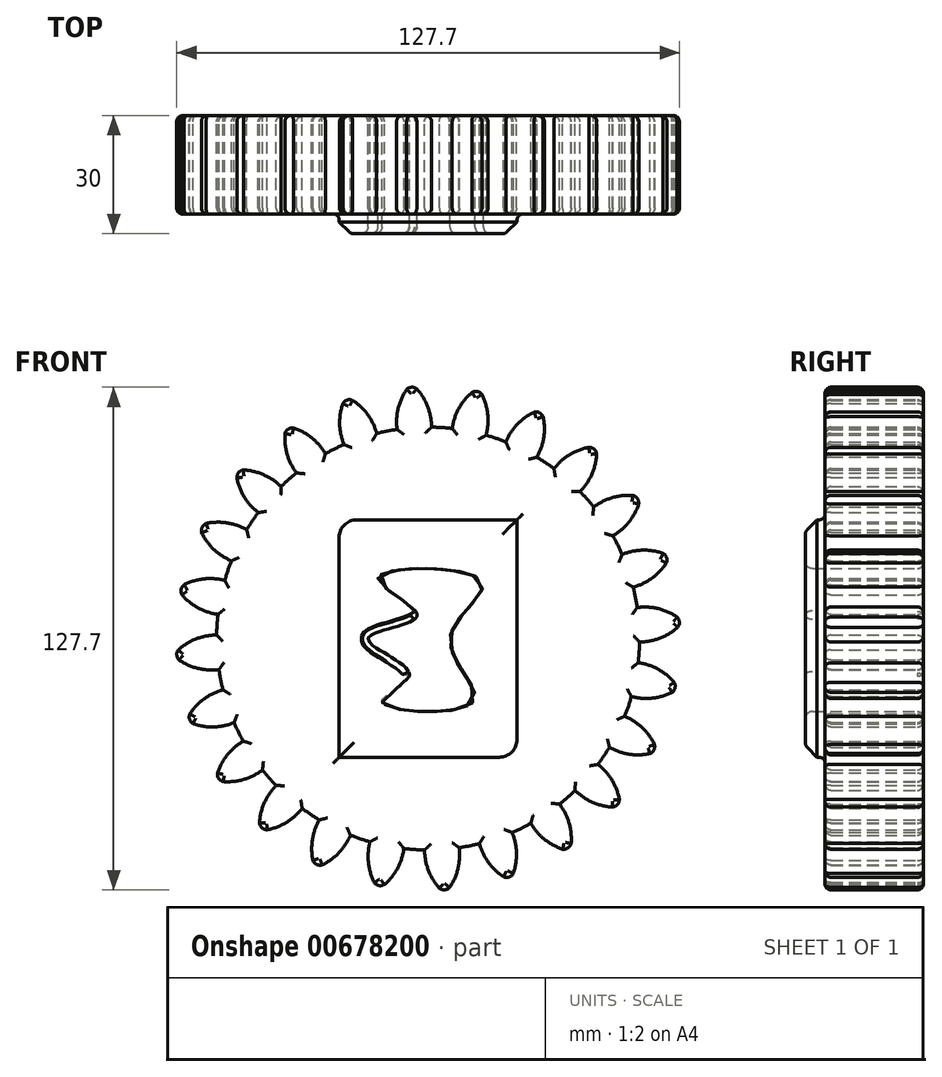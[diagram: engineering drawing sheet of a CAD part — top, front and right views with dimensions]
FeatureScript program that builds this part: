
annotation { "Feature Type Name" : "Feature", "Feature Type Description" : "" }
export const myFeature = defineFeature(function(context is Context, id is Id, definition is map)
    precondition{}
    {
        {
            var Q0;
            Q0=qCreatedBy(makeId("Front.planeOp"),FACE);
            var sketch = newSketch(context, id + "F0", { "sketchPlane" : qUnion([Q0])});
            skCircle(sketch, "E0", {"center": v(0, 0) * mm, "radius": 53.72 * mm});
            skCircle(sketch, "E1", {"center": v(0, 0) * mm, "radius": 58.67 * mm, "construction": true});
            skCircle(sketch, "E2", {"center": v(0, 0) * mm, "radius": 63.5 * mm, "construction": true});
            skLineSegment(sketch, "E3", {"start": v(0, 0) * mm, "end": v(0, 95.08) * mm, "construction": true});
            skLineSegment(sketch, "E4", {"start": v(0, 0) * mm, "end": v(-6.3, 96.03) * mm, "construction": true});
            skLineSegment(sketch, "E5", {"start": v(0, 63.95) * mm, "end": v(0, 63.5) * mm, "construction": true});
            skLineSegment(sketch, "E6", {"start": v(0, 58.67) * mm, "end": v(-63.97, 58.67) * mm, "construction": true});
            skLineSegment(sketch, "E7", {"start": v(0, 58.67) * mm, "end": v(-64.16, 35.32) * mm, "construction": true});
            skCircle(sketch, "E8", {"center": v(0, 0) * mm, "radius": 55.14 * mm, "construction": true});
            skCircle(sketch, "E9", {"center": v(0, 58.67) * mm, "radius": 14.6 * mm, "construction": true});
            skCircle(sketch, "E10", {"center": v(-13.72, 53.68) * mm, "radius": 14.6 * mm, "construction": true});
            skArc(sketch, "E11", {"start": v(0, 58.67) * mm, "mid": v(-1.2, 61.2) * mm, "end": v(-2.86, 63.44) * mm});
            skArc(sketch, "E12", {"start": v(0.88, 53.71) * mm, "mid": v(0.66, 56.23) * mm, "end": v(0, 58.67) * mm});
            skArc(sketch, "E13.MirrorCS", {"start": v(-7.66, 58.17) * mm, "mid": v(-6.8, 60.83) * mm, "end": v(-5.45, 63.27) * mm});
            skArc(sketch, "E14.MirrorCS", {"start": v(-7.88, 53.14) * mm, "mid": v(-7.99, 55.67) * mm, "end": v(-7.66, 58.17) * mm});
            skArc(sketch, "E15", {"start": v(-2.86, 63.44) * mm, "mid": v(-4.18, 63.85) * mm, "end": v(-5.45, 63.27) * mm});
            skLineSegment(sketch, "E16.bottom", {"start": v(22.6, 30.17) * mm, "end": v(-18.1, 30.17) * mm});
            skLineSegment(sketch, "E16.top", {"start": v(18.1, -30.17) * mm, "end": v(-22.6, -30.17) * mm});
            skLineSegment(sketch, "E16.left", {"start": v(22.6, 30.17) * mm, "end": v(22.6, -25.67) * mm});
            skLineSegment(sketch, "E16.right", {"start": v(-22.6, 25.67) * mm, "end": v(-22.6, -30.17) * mm});
            skFitSpline(sketch, "E17", {"points": [v(-11.69, -16.1) * mm, v(11.42, -16.15) * mm, v(5.58, 0) * mm, v(13.67, 14.65) * mm, v(-12.75, 15.4) * mm, v(-2.8, 5.83) * mm, v(-15.25, 0) * mm, v(-4.75, -9.12) * mm, v(-11.69, -16.1) * mm]});
            skPoint(sketch, "E18.visualSharp", {"position": v(-22.6, 30.17) * mm});
            skArc(sketch, "E18.filletArc", {"start": v(-18.1, 30.17) * mm, "mid": v(-21.28, 28.85) * mm, "end": v(-22.6, 25.67) * mm});
            skPoint(sketch, "E19.visualSharp", {"position": v(22.6, -30.17) * mm});
            skArc(sketch, "E19.filletArc", {"start": v(18.1, -30.17) * mm, "mid": v(21.28, -28.85) * mm, "end": v(22.6, -25.67) * mm});
            skSolve(sketch);
        }
        {
            var Q0;
            {var subQ0=sQuery(id+"F0.wireOp",EDGE,"E0");var subQ1=makeQuery(id+"F0.imprint","INTERSECT",VERTEX,{"derivedFrom":[subQ0,sQuery(id+"F0.wireOp",EDGE,"E12")]});Q0=makeQuery(id+"F0.imprint","IMPRINT",FACE,{"disambiguationData":[TD([[makeQuery(id+"F0.imprint","IMPRINT",EDGE,{"disambiguationData":[TD([[subQ1,-1.0]])],"derivedFrom":subQ0}),1.0]])]});}
            var Q1;
            Q1=makeQuery(id+"F0.imprint","IMPRINT",FACE,{"disambiguationData":[TD([[makeQuery(id+"F0.imprint","IMPRINT",EDGE,{"derivedFrom":sQuery(id+"F0.wireOp",EDGE,"E11")}),1.0]])]});
            extrude(context, id + "F1", {"entities" : qUnion([Q0, Q1]), "depth" : 25 * mm, "offsetDistance" : 25 * mm});
        }
        {
            var Q0;
            Q0=makeQuery(id+"F1.opExtrude","SWEPT_BODY",BODY,{"disambiguationData":[OSD([sQuery(id+"F0.wireOp",EDGE,"E0"),sQuery(id+"F0.wireOp",EDGE,"E11"),sQuery(id+"F0.wireOp",EDGE,"E12"),sQuery(id+"F0.wireOp",EDGE,"E13.MirrorCS"),sQuery(id+"F0.wireOp",EDGE,"E14.MirrorCS"),sQuery(id+"F0.wireOp",EDGE,"E15")])]});
            var Q1;
            Q1=makeQuery(id+"F1.opExtrude","SWEPT_FACE",FACE,{"disambiguationData":[OSD([sQuery(id+"F0.wireOp",EDGE,"E0")])]});
            circularPattern(context, id + "F2", {"entities" : qUnion([Q0]), "axis" : qUnion([Q1]), "angle" : 360 * degree, "instanceCount" : 24, "equalSpace" : true});
        }
        {
            var Q0;
            Q0=makeQuery(id+"F0.imprint","IMPRINT",FACE,{"disambiguationData":[TD([[makeQuery(id+"F0.imprint","IMPRINT",EDGE,{"derivedFrom":sQuery(id+"F0.wireOp",EDGE,"E16.bottom")}),1.0]])]});
            extrude(context, id + "F3", {"entities" : qUnion([Q0]), "operationType" : NewBodyOperationType.ADD, "depth" : 30 * mm, "offsetDistance" : 25 * mm});
        }
        {
            var Q0;
            Q0=makeQuery(id+"F3.opExtrude","CAP_EDGE",EDGE,{"disambiguationData":[OSD([sQuery(id+"F0.wireOp",EDGE,"E16.bottom")])],"isStart":false});
            var Q1;
            Q1=makeQuery(id+"F3.opExtrude","CAP_EDGE",EDGE,{"disambiguationData":[OSD([sQuery(id+"F0.wireOp",EDGE,"E16.right")])],"isStart":false});
            var Q2;
            Q2=makeQuery(id+"F3.opExtrude","CAP_EDGE",EDGE,{"disambiguationData":[OSD([sQuery(id+"F0.wireOp",EDGE,"E16.left")])],"isStart":false});
            var Q3;
            Q3=makeQuery(id+"F3.opExtrude","CAP_EDGE",EDGE,{"disambiguationData":[OSD([sQuery(id+"F0.wireOp",EDGE,"E16.top")])],"isStart":false});
            var Q4;
            Q4=makeQuery(id+"F3.opExtrude","CAP_EDGE",EDGE,{"disambiguationData":[OSD([sQuery(id+"F0.wireOp",EDGE,"E16.bottom")])],"isStart":true});
            var Q5;
            Q5=makeQuery(id+"F3.opExtrude","CAP_EDGE",EDGE,{"disambiguationData":[OSD([sQuery(id+"F0.wireOp",EDGE,"E16.top")])],"isStart":true});
            chamfer(context, id + "F4", {"entities" : qUnion([Q0, Q1, Q2, Q3, Q4, Q5]), "width" : 3 * mm, "tangentPropagation" : true});
        }
        {
            var Q0;
            {var subQ0=sQuery(id+"F0.wireOp",EDGE,"E19.filletArc");var subQ1=sQuery(id+"F0.wireOp",EDGE,"E18.filletArc");var subQ2=sQuery(id+"F0.wireOp",EDGE,"E16.right");var subQ3=sQuery(id+"F0.wireOp",EDGE,"E16.left");var subQ4=sQuery(id+"F0.wireOp",EDGE,"E16.top");var subQ5=sQuery(id+"F0.wireOp",EDGE,"E16.bottom");var subQ6=makeQuery(id+"F1.opExtrude","CAP_FACE",FACE,{"disambiguationData":[OSD([sQuery(id+"F0.wireOp",EDGE,"E0"),sQuery(id+"F0.wireOp",EDGE,"E11"),sQuery(id+"F0.wireOp",EDGE,"E12"),sQuery(id+"F0.wireOp",EDGE,"E13.MirrorCS"),sQuery(id+"F0.wireOp",EDGE,"E14.MirrorCS"),sQuery(id+"F0.wireOp",EDGE,"E15"),subQ5,subQ4,subQ3,subQ2,subQ1,subQ0])],"isStart":true});Q0=makeQuery(id+"F3.boolean.opBoolean","MERGE",FACE,{"derivedFrom":[subQ6,makeQuery(id+"F2.opPattern","COPY",FACE,{"derivedFrom":subQ6,"instanceName":"1"}),makeQuery(id+"F2.opPattern","COPY",FACE,{"derivedFrom":subQ6,"instanceName":"2"}),makeQuery(id+"F2.opPattern","COPY",FACE,{"derivedFrom":subQ6,"instanceName":"3"}),makeQuery(id+"F2.opPattern","COPY",FACE,{"derivedFrom":subQ6,"instanceName":"4"}),makeQuery(id+"F2.opPattern","COPY",FACE,{"derivedFrom":subQ6,"instanceName":"5"}),makeQuery(id+"F2.opPattern","COPY",FACE,{"derivedFrom":subQ6,"instanceName":"6"}),makeQuery(id+"F2.opPattern","COPY",FACE,{"derivedFrom":subQ6,"instanceName":"7"}),makeQuery(id+"F2.opPattern","COPY",FACE,{"derivedFrom":subQ6,"instanceName":"8"}),makeQuery(id+"F2.opPattern","COPY",FACE,{"derivedFrom":subQ6,"instanceName":"9"}),makeQuery(id+"F2.opPattern","COPY",FACE,{"derivedFrom":subQ6,"instanceName":"10"}),makeQuery(id+"F2.opPattern","COPY",FACE,{"derivedFrom":subQ6,"instanceName":"11"}),makeQuery(id+"F2.opPattern","COPY",FACE,{"derivedFrom":subQ6,"instanceName":"12"}),makeQuery(id+"F2.opPattern","COPY",FACE,{"derivedFrom":subQ6,"instanceName":"13"}),makeQuery(id+"F2.opPattern","COPY",FACE,{"derivedFrom":subQ6,"instanceName":"14"}),makeQuery(id+"F2.opPattern","COPY",FACE,{"derivedFrom":subQ6,"instanceName":"15"}),makeQuery(id+"F2.opPattern","COPY",FACE,{"derivedFrom":subQ6,"instanceName":"16"}),makeQuery(id+"F2.opPattern","COPY",FACE,{"derivedFrom":subQ6,"instanceName":"17"}),makeQuery(id+"F2.opPattern","COPY",FACE,{"derivedFrom":subQ6,"instanceName":"18"}),makeQuery(id+"F2.opPattern","COPY",FACE,{"derivedFrom":subQ6,"instanceName":"19"}),makeQuery(id+"F2.opPattern","COPY",FACE,{"derivedFrom":subQ6,"instanceName":"20"}),makeQuery(id+"F2.opPattern","COPY",FACE,{"derivedFrom":subQ6,"instanceName":"21"}),makeQuery(id+"F2.opPattern","COPY",FACE,{"derivedFrom":subQ6,"instanceName":"22"}),makeQuery(id+"F2.opPattern","COPY",FACE,{"derivedFrom":subQ6,"instanceName":"23"}),makeQuery(id+"F3.opExtrude","CAP_FACE",FACE,{"disambiguationData":[OSD([subQ5,subQ4,subQ3,subQ2,sQuery(id+"F0.wireOp",EDGE,"E17"),subQ1,subQ0])],"isStart":true})]});}
            var Q1;
            {var subQ0=makeQuery(id+"F1.opExtrude","CAP_FACE",FACE,{"disambiguationData":[OSD([sQuery(id+"F0.wireOp",EDGE,"E0"),sQuery(id+"F0.wireOp",EDGE,"E11"),sQuery(id+"F0.wireOp",EDGE,"E12"),sQuery(id+"F0.wireOp",EDGE,"E13.MirrorCS"),sQuery(id+"F0.wireOp",EDGE,"E14.MirrorCS"),sQuery(id+"F0.wireOp",EDGE,"E15"),sQuery(id+"F0.wireOp",EDGE,"E16.bottom"),sQuery(id+"F0.wireOp",EDGE,"E16.top"),sQuery(id+"F0.wireOp",EDGE,"E16.left"),sQuery(id+"F0.wireOp",EDGE,"E16.right"),sQuery(id+"F0.wireOp",EDGE,"E18.filletArc"),sQuery(id+"F0.wireOp",EDGE,"E19.filletArc")])],"isStart":false});Q1=makeQuery(id+"F3.boolean.opBoolean","MERGE",FACE,{"derivedFrom":[subQ0,makeQuery(id+"F2.opPattern","COPY",FACE,{"derivedFrom":subQ0,"instanceName":"1"}),makeQuery(id+"F2.opPattern","COPY",FACE,{"derivedFrom":subQ0,"instanceName":"2"}),makeQuery(id+"F2.opPattern","COPY",FACE,{"derivedFrom":subQ0,"instanceName":"3"}),makeQuery(id+"F2.opPattern","COPY",FACE,{"derivedFrom":subQ0,"instanceName":"4"}),makeQuery(id+"F2.opPattern","COPY",FACE,{"derivedFrom":subQ0,"instanceName":"5"}),makeQuery(id+"F2.opPattern","COPY",FACE,{"derivedFrom":subQ0,"instanceName":"6"}),makeQuery(id+"F2.opPattern","COPY",FACE,{"derivedFrom":subQ0,"instanceName":"7"}),makeQuery(id+"F2.opPattern","COPY",FACE,{"derivedFrom":subQ0,"instanceName":"8"}),makeQuery(id+"F2.opPattern","COPY",FACE,{"derivedFrom":subQ0,"instanceName":"9"}),makeQuery(id+"F2.opPattern","COPY",FACE,{"derivedFrom":subQ0,"instanceName":"10"}),makeQuery(id+"F2.opPattern","COPY",FACE,{"derivedFrom":subQ0,"instanceName":"11"}),makeQuery(id+"F2.opPattern","COPY",FACE,{"derivedFrom":subQ0,"instanceName":"12"}),makeQuery(id+"F2.opPattern","COPY",FACE,{"derivedFrom":subQ0,"instanceName":"13"}),makeQuery(id+"F2.opPattern","COPY",FACE,{"derivedFrom":subQ0,"instanceName":"14"}),makeQuery(id+"F2.opPattern","COPY",FACE,{"derivedFrom":subQ0,"instanceName":"15"}),makeQuery(id+"F2.opPattern","COPY",FACE,{"derivedFrom":subQ0,"instanceName":"16"}),makeQuery(id+"F2.opPattern","COPY",FACE,{"derivedFrom":subQ0,"instanceName":"17"}),makeQuery(id+"F2.opPattern","COPY",FACE,{"derivedFrom":subQ0,"instanceName":"18"}),makeQuery(id+"F2.opPattern","COPY",FACE,{"derivedFrom":subQ0,"instanceName":"19"}),makeQuery(id+"F2.opPattern","COPY",FACE,{"derivedFrom":subQ0,"instanceName":"20"}),makeQuery(id+"F2.opPattern","COPY",FACE,{"derivedFrom":subQ0,"instanceName":"21"}),makeQuery(id+"F2.opPattern","COPY",FACE,{"derivedFrom":subQ0,"instanceName":"22"}),makeQuery(id+"F2.opPattern","COPY",FACE,{"derivedFrom":subQ0,"instanceName":"23"})]});}
            fillet(context, id + "F5", {"entities" : qUnion([Q0, Q1]), "radius" : 1.5 * mm, "tangentPropagation" : true, "allowEdgeOverflow" : false});
        }
        {
            var Q0;
            Q0=makeQuery(id+"F3.opExtrude","SWEPT_FACE",FACE,{"disambiguationData":[OSD([sQuery(id+"F0.wireOp",EDGE,"E17")])]});
            var Q1;
            {var subQ0=sQuery(id+"F0.wireOp",EDGE,"E16.bottom");Q1=makeQuery(id+"F4.opChamfer","BLEND_EDGE",EDGE,{"blendedFrom":[makeQuery(id+"F3.opExtrude","CAP_EDGE",EDGE,{"disambiguationData":[OSD([subQ0])],"isStart":false}),makeQuery(id+"F3.opExtrude","CAP_FACE",FACE,{"disambiguationData":[OSD([subQ0,sQuery(id+"F0.wireOp",EDGE,"E16.top"),sQuery(id+"F0.wireOp",EDGE,"E16.left"),sQuery(id+"F0.wireOp",EDGE,"E16.right"),sQuery(id+"F0.wireOp",EDGE,"E17"),sQuery(id+"F0.wireOp",EDGE,"E18.filletArc"),sQuery(id+"F0.wireOp",EDGE,"E19.filletArc")])],"isStart":false})],"blendedInto":[makeQuery(id+"F3.opExtrude","CAP_FACE",FACE,{"disambiguationData":[OSD([subQ0,sQuery(id+"F0.wireOp",EDGE,"E16.top"),sQuery(id+"F0.wireOp",EDGE,"E16.left"),sQuery(id+"F0.wireOp",EDGE,"E16.right"),sQuery(id+"F0.wireOp",EDGE,"E17"),sQuery(id+"F0.wireOp",EDGE,"E18.filletArc"),sQuery(id+"F0.wireOp",EDGE,"E19.filletArc")])],"isStart":false})]});}
            var Q2;
            {var subQ0=sQuery(id+"F0.wireOp",EDGE,"E16.left");Q2=makeQuery(id+"F4.opChamfer","BLEND_EDGE",EDGE,{"blendedFrom":[makeQuery(id+"F3.opExtrude","CAP_EDGE",EDGE,{"disambiguationData":[OSD([subQ0])],"isStart":false}),makeQuery(id+"F3.opExtrude","CAP_FACE",FACE,{"disambiguationData":[OSD([sQuery(id+"F0.wireOp",EDGE,"E16.bottom"),sQuery(id+"F0.wireOp",EDGE,"E16.top"),subQ0,sQuery(id+"F0.wireOp",EDGE,"E16.right"),sQuery(id+"F0.wireOp",EDGE,"E17"),sQuery(id+"F0.wireOp",EDGE,"E18.filletArc"),sQuery(id+"F0.wireOp",EDGE,"E19.filletArc")])],"isStart":false})],"blendedInto":[makeQuery(id+"F3.opExtrude","CAP_FACE",FACE,{"disambiguationData":[OSD([sQuery(id+"F0.wireOp",EDGE,"E16.bottom"),sQuery(id+"F0.wireOp",EDGE,"E16.top"),subQ0,sQuery(id+"F0.wireOp",EDGE,"E16.right"),sQuery(id+"F0.wireOp",EDGE,"E17"),sQuery(id+"F0.wireOp",EDGE,"E18.filletArc"),sQuery(id+"F0.wireOp",EDGE,"E19.filletArc")])],"isStart":false})]});}
            var Q3;
            {var subQ0=sQuery(id+"F0.wireOp",EDGE,"E16.top");Q3=makeQuery(id+"F4.opChamfer","BLEND_EDGE",EDGE,{"blendedFrom":[makeQuery(id+"F3.opExtrude","CAP_EDGE",EDGE,{"disambiguationData":[OSD([subQ0])],"isStart":false}),makeQuery(id+"F3.opExtrude","CAP_FACE",FACE,{"disambiguationData":[OSD([sQuery(id+"F0.wireOp",EDGE,"E16.bottom"),subQ0,sQuery(id+"F0.wireOp",EDGE,"E16.left"),sQuery(id+"F0.wireOp",EDGE,"E16.right"),sQuery(id+"F0.wireOp",EDGE,"E17"),sQuery(id+"F0.wireOp",EDGE,"E18.filletArc"),sQuery(id+"F0.wireOp",EDGE,"E19.filletArc")])],"isStart":false})],"blendedInto":[makeQuery(id+"F3.opExtrude","CAP_FACE",FACE,{"disambiguationData":[OSD([sQuery(id+"F0.wireOp",EDGE,"E16.bottom"),subQ0,sQuery(id+"F0.wireOp",EDGE,"E16.left"),sQuery(id+"F0.wireOp",EDGE,"E16.right"),sQuery(id+"F0.wireOp",EDGE,"E17"),sQuery(id+"F0.wireOp",EDGE,"E18.filletArc"),sQuery(id+"F0.wireOp",EDGE,"E19.filletArc")])],"isStart":false})]});}
            var Q4;
            {var subQ0=sQuery(id+"F0.wireOp",EDGE,"E16.right");Q4=makeQuery(id+"F4.opChamfer","BLEND_EDGE",EDGE,{"blendedFrom":[makeQuery(id+"F3.opExtrude","CAP_EDGE",EDGE,{"disambiguationData":[OSD([subQ0])],"isStart":false}),makeQuery(id+"F3.opExtrude","CAP_FACE",FACE,{"disambiguationData":[OSD([sQuery(id+"F0.wireOp",EDGE,"E16.bottom"),sQuery(id+"F0.wireOp",EDGE,"E16.top"),sQuery(id+"F0.wireOp",EDGE,"E16.left"),subQ0,sQuery(id+"F0.wireOp",EDGE,"E17"),sQuery(id+"F0.wireOp",EDGE,"E18.filletArc"),sQuery(id+"F0.wireOp",EDGE,"E19.filletArc")])],"isStart":false})],"blendedInto":[makeQuery(id+"F3.opExtrude","CAP_FACE",FACE,{"disambiguationData":[OSD([sQuery(id+"F0.wireOp",EDGE,"E16.bottom"),sQuery(id+"F0.wireOp",EDGE,"E16.top"),sQuery(id+"F0.wireOp",EDGE,"E16.left"),subQ0,sQuery(id+"F0.wireOp",EDGE,"E17"),sQuery(id+"F0.wireOp",EDGE,"E18.filletArc"),sQuery(id+"F0.wireOp",EDGE,"E19.filletArc")])],"isStart":false})]});}
            fillet(context, id + "F6", {"entities" : qUnion([Q0, Q1, Q2, Q3, Q4]), "radius" : 1.75 * mm, "tangentPropagation" : true, "allowEdgeOverflow" : false});
        }
    });
